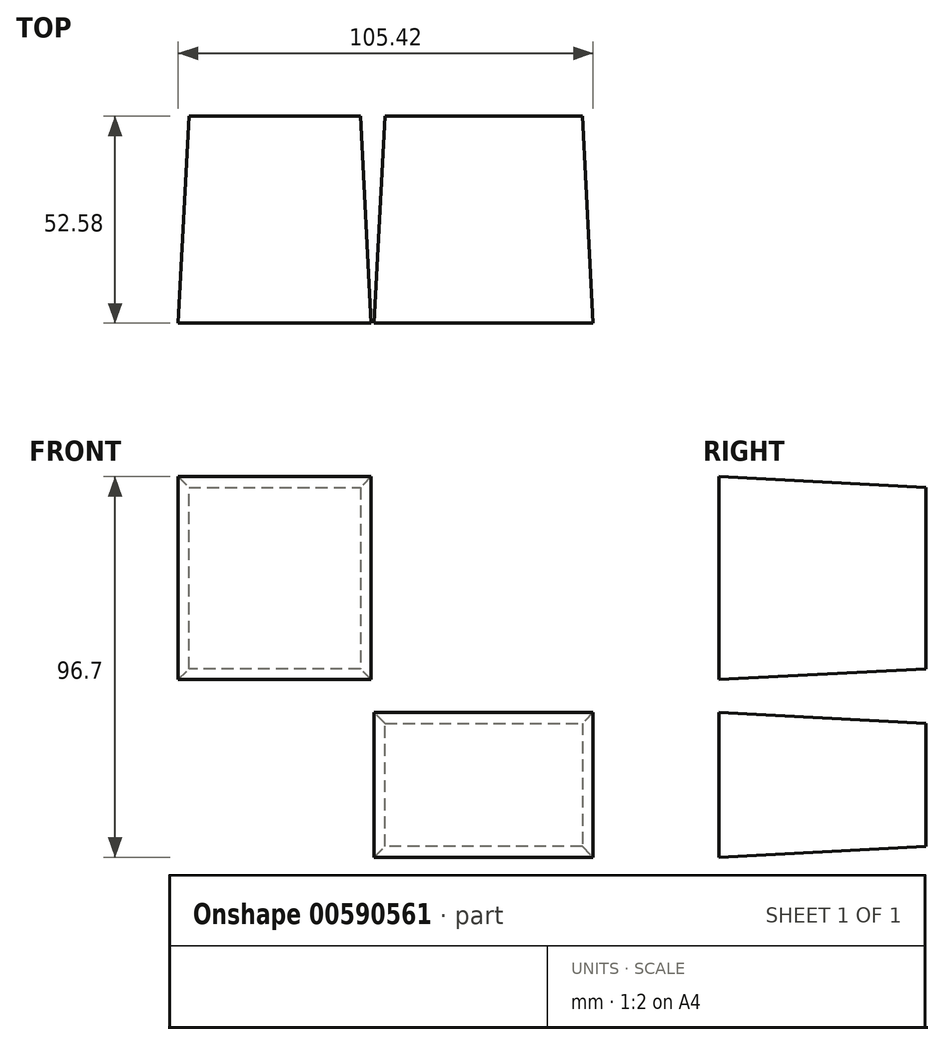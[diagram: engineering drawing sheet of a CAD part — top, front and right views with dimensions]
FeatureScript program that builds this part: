
annotation { "Feature Type Name" : "Feature", "Feature Type Description" : "" }
export const myFeature = defineFeature(function(context is Context, id is Id, definition is map)
    precondition{}
    {
        {
            var Q0;
            Q0=qCreatedBy(makeId("Front.planeOp"),FACE);
            var sketch = newSketch(context, id + "F0", { "sketchPlane" : qUnion([Q0])});
            skLineSegment(sketch, "E0", {"start": v(-58.04, 59.91) * mm, "end": v(-14.5, 59.91) * mm});
            skLineSegment(sketch, "E1", {"start": v(-14.5, 59.91) * mm, "end": v(-14.5, 13.88) * mm});
            skLineSegment(sketch, "E2", {"start": v(-14.5, 13.88) * mm, "end": v(-58.04, 13.88) * mm});
            skLineSegment(sketch, "E3", {"start": v(-58.04, 13.88) * mm, "end": v(-58.04, 59.91) * mm});
            skLineSegment(sketch, "E4.bottom", {"start": v(-8.24, 0) * mm, "end": v(41.88, 0) * mm});
            skLineSegment(sketch, "E4.top", {"start": v(-8.24, -31.27) * mm, "end": v(41.88, -31.27) * mm});
            skLineSegment(sketch, "E4.left", {"start": v(-8.24, 0) * mm, "end": v(-8.24, -31.27) * mm});
            skLineSegment(sketch, "E4.right", {"start": v(41.88, 0) * mm, "end": v(41.88, -31.27) * mm});
            skArc(sketch, "E5", {"start": v(19.13, 0) * mm, "mid": v(27.8, 44.27) * mm, "end": v(-14.5, 59.91) * mm});
            skSolve(sketch);
        }
        {
            var Q0;
            Q0=makeQuery(id+"F0.imprint","IMPRINT",FACE,{"disambiguationData":[TD([[makeQuery(id+"F0.imprint","IMPRINT",EDGE,{"derivedFrom":sQuery(id+"F0.wireOp",EDGE,"E4.top")}),1.0]])]});
            var Q1;
            Q1=makeQuery(id+"F0.imprint","IMPRINT",FACE,{"disambiguationData":[TD([[makeQuery(id+"F0.imprint","IMPRINT",EDGE,{"derivedFrom":sQuery(id+"F0.wireOp",EDGE,"E0")}),-1.0]])]});
            extrude(context, id + "F1", {"entities" : qUnion([Q0, Q1]), "depth" : 52.58 * mm, "offsetDistance" : 25.4 * mm, "hasDraft" : true, "draftAngle" : 3 * degree});
        }
    });
